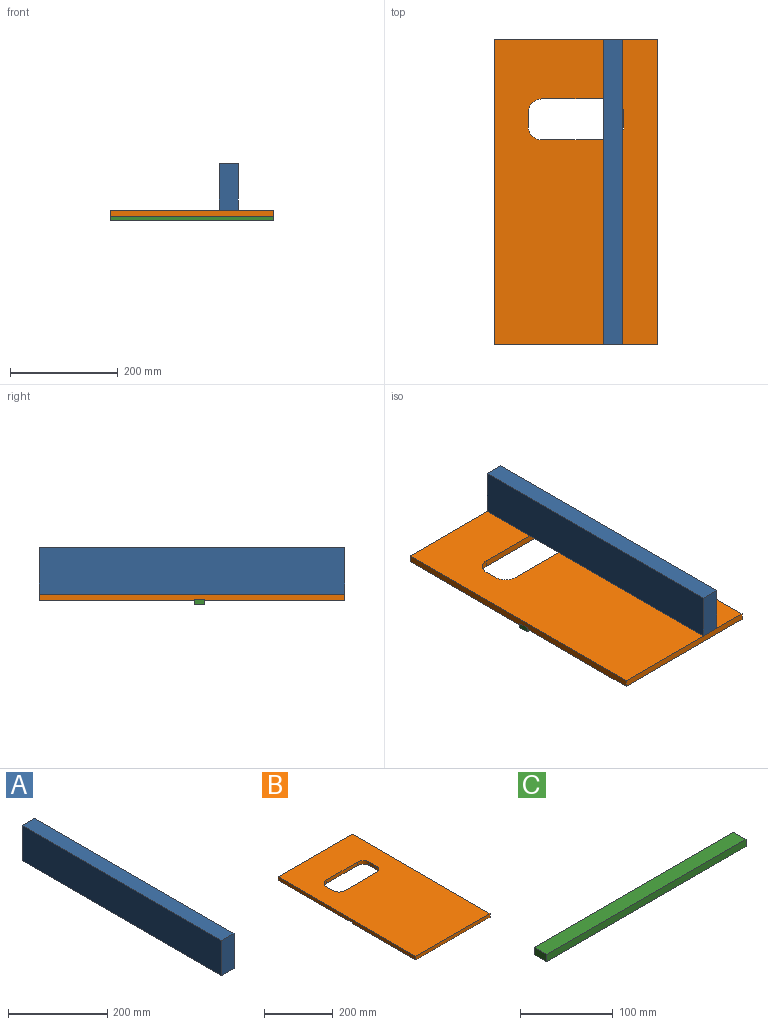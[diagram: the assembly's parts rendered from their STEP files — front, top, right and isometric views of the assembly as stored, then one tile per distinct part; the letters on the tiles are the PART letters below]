
ASSEMBLY  parts=3 mates=2
PART A: 6 faces, bbox 35.6x568.3x86.4 mm
  f0: plane 86.36x35.56mm, normal (0,1,0), area 3071mm2, adj f1,f3,f4,f5
  f1: plane 568.33x86.36mm, normal (-1,0,0), area 49080.5mm2, adj f0,f2,f3,f4
  f2: plane 86.36x35.56mm, normal (0,-1,0), area 3071mm2, adj f1,f3,f4,f5
  f3: plane 568.33x35.56mm, normal (0,0,1), area 20209.6mm2, adj f0,f1,f2,f5
  f4: plane 568.33x35.56mm, normal (0,0,-1), area 20209.6mm2, adj f0,f1,f2,f5
  f5: plane 568.33x86.36mm, normal (1,0,0), area 49080.5mm2, adj f0,f2,f3,f4
PART B: 18 faces, bbox 304.8x568.3x12.7 mm
  f0: plane 304.8x288.93mm, normal (0,0,-1), area 75069.8mm2, adj f3,f5,f6,f9,f10,f11,f12,f13
  f1: plane 304.8x12.7mm, normal (0,-1,0), area 3871mm2, adj f2,f4,f5,f6
  f2: plane 304.8x260.35mm, normal (0,0,-1), area 79354.7mm2, adj f1,f5,f6,f8
  f3: plane 304.8x12.7mm, normal (0,1,0), area 3871mm2, adj f0,f4,f5,f6
  f4: plane 568.33x304.8mm, normal (0,0,1), area 160230.9mm2, adj f1,f3,f5,f6,f10,f11,f12,f13
  f5: plane 568.33x12.7mm, normal (1,0,0), area 7157.2mm2, adj f0,f1,f2,f3,f4,f7,f8,f9
  f6: plane 568.33x12.7mm, normal (-1,0,0), area 7157.2mm2, adj f0,f1,f2,f3,f4,f7,f8,f9
  f7: plane 304.8x19.05mm, normal (0,0,-1), area 5806.4mm2, adj f5,f6,f8,f9
  f8: plane 304.8x3.18mm, normal (0,1,0), area 967.7mm2, adj f2,f5,f6,f7
  f9: plane 304.8x3.18mm, normal (0,-1,0), area 967.7mm2, adj f0,f5,f6,f7
  f10: cylinder r=25.4mm len=25.4mm, axis (0,0,-1), area 506.7mm2, adj f0,f4,f11,f16
  f11: plane 25.4x12.7mm, normal (1,0,0), area 322.6mm2, adj f0,f4,f10,f12
  f12: cylinder r=25.4mm len=25.4mm, axis (0,0,-1), area 506.7mm2, adj f0,f4,f11,f13
  f13: plane 127x12.7mm, normal (0,1,0), area 1612.9mm2, adj f0,f4,f12,f14
  f14: cylinder r=25.4mm len=25.4mm, axis (0,0,-1), area 506.7mm2, adj f0,f4,f13,f15
  f15: plane 25.4x12.7mm, normal (-1,0,0), area 322.6mm2, adj f0,f4,f14,f17
  f16: plane 127x12.7mm, normal (0,-1,0), area 1612.9mm2, adj f0,f4,f10,f17
  f17: cylinder r=25.4mm len=25.4mm, axis (0,0,-1), area 506.7mm2, adj f0,f4,f15,f16
PART C: 6 faces, bbox 304.8x19.1x9.5 mm
  f0: plane 19.05x9.53mm, normal (1,0,0), area 181.5mm2, adj f1,f3,f4,f5
  f1: plane 304.8x9.53mm, normal (0,-1,0), area 2903.2mm2, adj f0,f2,f3,f4
  f2: plane 19.05x9.53mm, normal (-1,0,0), area 181.5mm2, adj f1,f3,f4,f5
  f3: plane 304.8x19.05mm, normal (0,0,-1), area 5806.4mm2, adj f0,f1,f2,f5
  f4: plane 304.8x19.05mm, normal (0,0,1), area 5806.4mm2, adj f0,f1,f2,f5
  f5: plane 304.8x9.53mm, normal (0,1,0), area 2903.2mm2, adj f0,f2,f3,f4
PLACE A t=(-50.47,37.59,161)mm
PLACE B t=(-50.47,37.59,161)mm
PLACE C t=(-50.47,37.59,161)mm
MATE fastened B.f4 <-> A.f4  axis (0,0,1) through (-50.47,37.59,173.7)mm
MATE fastened C.f4 <-> B.f7  axis (0,0,1) through (101.93,307.46,164.17)mm
